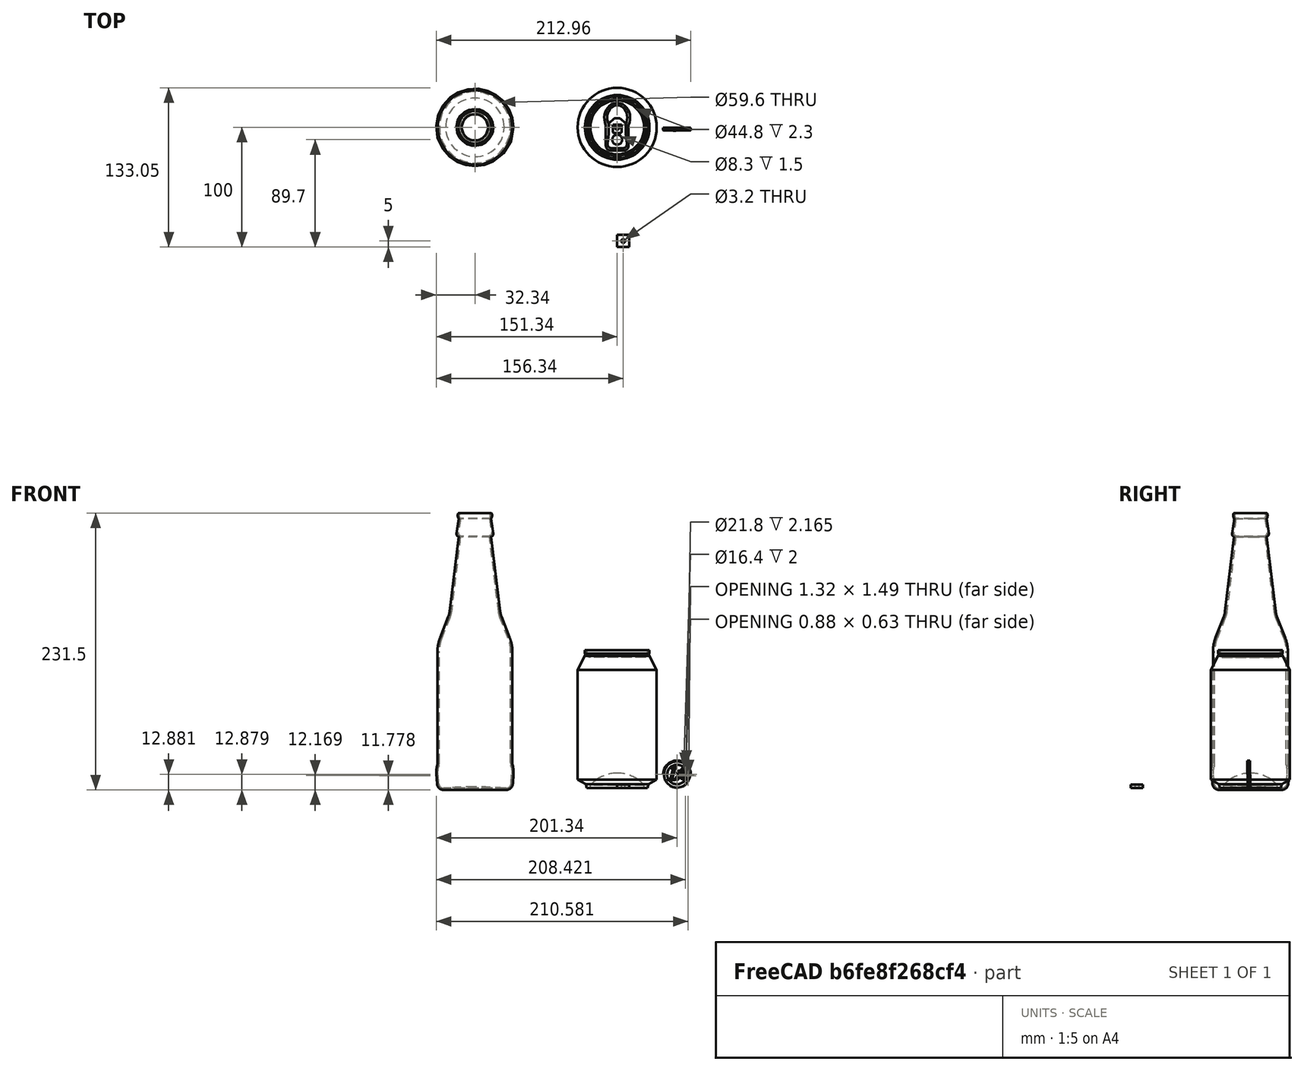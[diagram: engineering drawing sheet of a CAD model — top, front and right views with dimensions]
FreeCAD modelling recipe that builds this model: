
FCSTD DOCUMENT  (FreeCAD 0.20R29410 (Git))
Label: 1
License: All rights reserved
LicenseURL: http://en.wikipedia.org/wiki/All_rights_reserved
objects: Part::Feature×3, Part::Box×1, Part::Cylinder×1, Part::Cut×1
note: 6 computed .brp shape members not serialized (recipe doc carries the construction recipe); baked Part::Feature solids carry a one-line shape summary decoded from their .brp

FEATURE [Part::Feature] Compound001  label="Euro-coin"
  Placement = pos=(50,99.808,10.9983) rot=(1,0,0;1.58825rad)
  shape: bbox 23.25 x 2.737 x 23.28 mm, 903 faces, 22 solids (baked)
FEATURE [Part::Feature] Thickness001  label="Bottle"
  Placement = pos=(-119,100,0) rot=(0,0,1;0rad)
  shape: bbox 71.75 x 74.3 x 235 mm, 40 faces (baked)
FEATURE [Part::Feature] Fusion001  label="Can"
  Placement = pos=(0,100,0) rot=(0,0,1;0rad)
  shape: bbox 66.1 x 66.1 x 115.2 mm, 53 faces (baked)
FEATURE [Part::Box] Box  label="Cubo"
  AttacherType = Attacher::AttachEngine3D
  Height = 3
  Length = 10
  Width = 10
FEATURE [Part::Cylinder] Cylinder  label="Cilindro"
  Angle = 360
  AttacherType = Attacher::AttachEngine3D
  FirstAngle = 0
  Height = 10
  Placement = pos=(5,5,-3) rot=(0,0,1;0rad)
  Radius = 1.6
  SecondAngle = 0
FEATURE [Part::Cut] Cut
  Base = -> Box
  Tool = -> Cylinder
